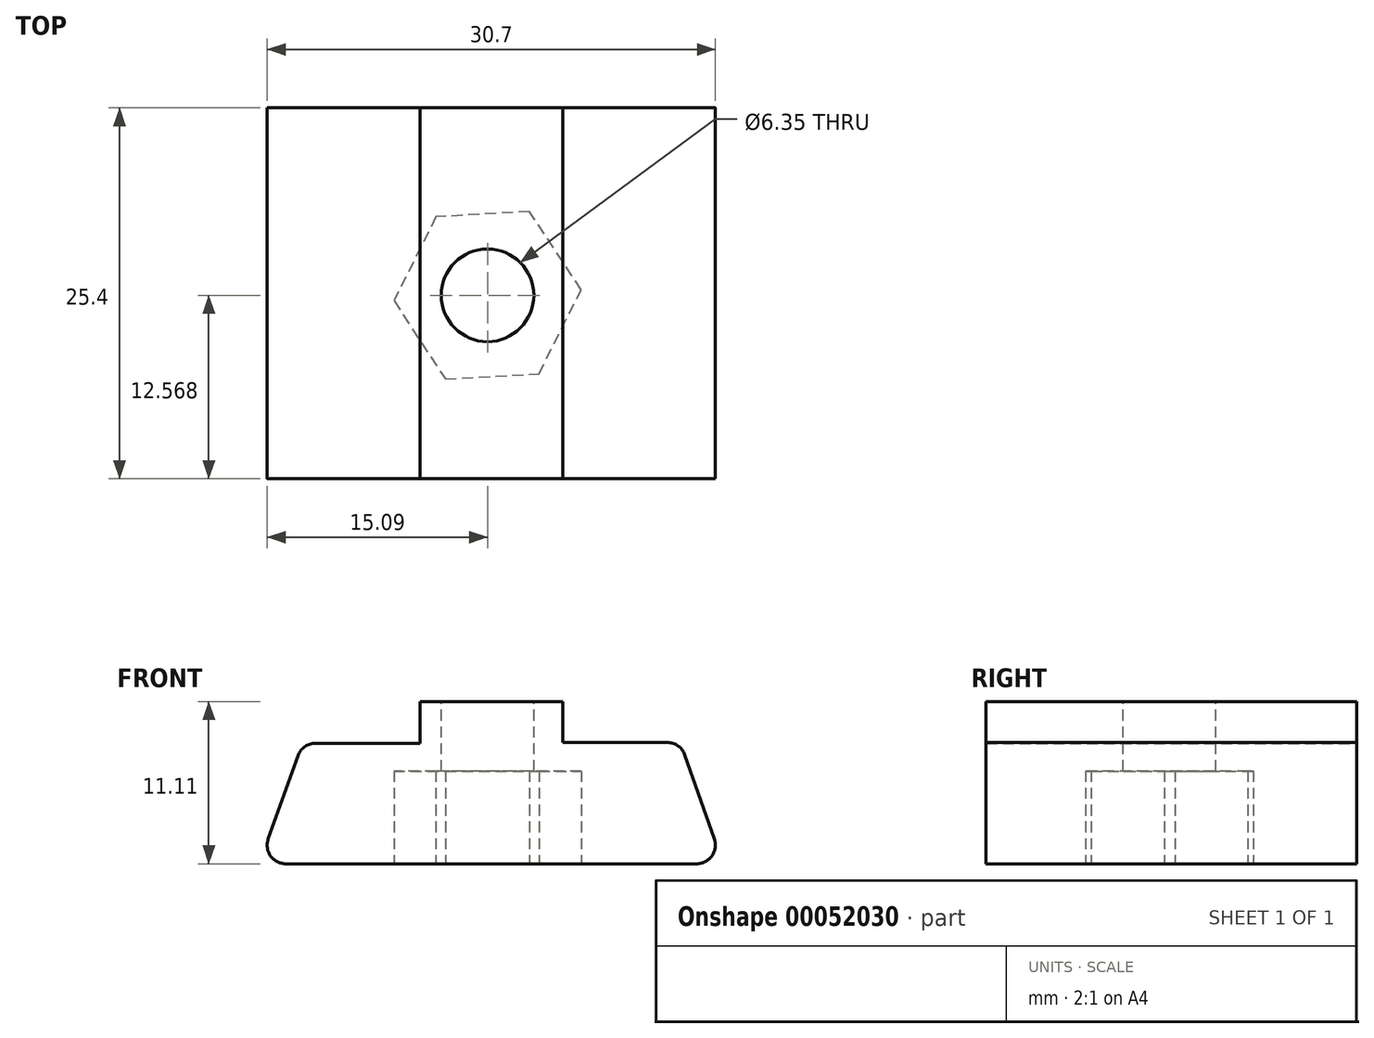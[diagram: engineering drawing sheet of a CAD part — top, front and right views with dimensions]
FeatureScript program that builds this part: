
annotation { "Feature Type Name" : "Feature", "Feature Type Description" : "" }
export const myFeature = defineFeature(function(context is Context, id is Id, definition is map)
    precondition{}
    {
        {
            var Q0;
            Q0=qCreatedBy(makeId("Front.planeOp"),FACE);
            var sketch = newSketch(context, id + "F0", { "sketchPlane" : qUnion([Q0])});
            skLineSegment(sketch, "E0", {"start": v(-15.62, 0) * mm, "end": v(16.13, 0) * mm});
            skLineSegment(sketch, "E1", {"start": v(16.13, 0) * mm, "end": v(13.23, 8.3) * mm});
            skLineSegment(sketch, "E2", {"start": v(13.23, 8.3) * mm, "end": v(5.16, 8.3) * mm});
            skLineSegment(sketch, "E3", {"start": v(5.16, 8.3) * mm, "end": v(5.16, 11.11) * mm});
            skLineSegment(sketch, "E4", {"start": v(5.16, 11.11) * mm, "end": v(-4.62, 11.11) * mm});
            skLineSegment(sketch, "E5", {"start": v(-4.62, 11.11) * mm, "end": v(-4.62, 8.26) * mm});
            skLineSegment(sketch, "E6", {"start": v(-4.62, 8.26) * mm, "end": v(-12.68, 8.25) * mm});
            skLineSegment(sketch, "E7", {"start": v(-12.68, 8.26) * mm, "end": v(-15.62, 0) * mm});
            skSolve(sketch);
        }
        {
            var Q0;
            Q0 = qSketchRegion(id + "F0", true);
            extrude(context, id + "F1", {"entities" : qUnion([Q0]), "depth" : 25.4 * mm});
        }
        {
            var Q0;
            Q0=makeQuery(id+"F1.opExtrude","SWEPT_FACE",FACE,{"disambiguationData":[OSD([sQuery(id+"F0.wireOp",EDGE,"E4")])]});
            var sketch = newSketch(context, id + "F2", { "sketchPlane" : qUnion([Q0])});
            skCircle(sketch, "E8", {"center": v(0, -12.83) * mm, "radius": 2.25 * mm});
            skSolve(sketch);
        }
        {
            var Q0;
            Q0=sQuery(id+"F2.wireOp",VERTEX,"E8.center");
            var Q1;
            Q1=makeQuery(id+"F1.opExtrude","SWEPT_BODY",BODY,{"disambiguationData":[OSD([sQuery(id+"F0.wireOp",EDGE,"E0"),sQuery(id+"F0.wireOp",EDGE,"E1"),sQuery(id+"F0.wireOp",EDGE,"E2"),sQuery(id+"F0.wireOp",EDGE,"E3"),sQuery(id+"F0.wireOp",EDGE,"E4"),sQuery(id+"F0.wireOp",EDGE,"E5"),sQuery(id+"F0.wireOp",EDGE,"E6"),sQuery(id+"F0.wireOp",EDGE,"E7")])]});
            hole(context, id + "F3", {"style" : HoleStyle.SIMPLE, "holeDiameter" : 6.35 * mm, "endStyle" : HoleEndStyle.THROUGH, "locations" : qUnion([Q0]), "scope" : qUnion([Q1])});
        }
        {
            var Q0;
            Q0=makeQuery(id+"F1.opExtrude","SWEPT_FACE",FACE,{"disambiguationData":[OSD([sQuery(id+"F0.wireOp",EDGE,"E0")])]});
            var sketch = newSketch(context, id + "F4", { "sketchPlane" : qUnion([Q0])});
            skCircle(sketch, "E9.cCircle", {"center": v(0, 12.83) * mm, "radius": 6.42 * mm, "construction": true});
            skLineSegment(sketch, "E9.0", {"start": v(-3.53, 7.46) * mm, "end": v(-6.41, 13.2) * mm});
            skLineSegment(sketch, "E9.1", {"start": v(-6.41, 13.2) * mm, "end": v(-2.89, 18.57) * mm});
            skLineSegment(sketch, "E9.2", {"start": v(-2.89, 18.57) * mm, "end": v(3.53, 18.2) * mm});
            skLineSegment(sketch, "E9.3", {"start": v(3.53, 18.2) * mm, "end": v(6.41, 12.46) * mm});
            skLineSegment(sketch, "E9.4", {"start": v(6.41, 12.46) * mm, "end": v(2.89, 7.1) * mm});
            skLineSegment(sketch, "E9.5", {"start": v(2.89, 7.1) * mm, "end": v(-3.53, 7.46) * mm});
            skSolve(sketch);
        }
        {
            var Q0;
            Q0=makeQuery(id+"F4.imprint","IMPRINT",FACE,{"disambiguationData":[TD([[makeQuery(id+"F4.imprint","IMPRINT",EDGE,{"derivedFrom":makeQuery(id+"F3.hole-0.boolean.opBoolean","INTERSECT",EDGE,{"derivedFrom":[makeQuery(id+"F1.opExtrude","SWEPT_FACE",FACE,{"disambiguationData":[OSD([sQuery(id+"F0.wireOp",EDGE,"E0")])]}),makeQuery(id+"F3.hole-0.opRevolve","SWEPT_FACE",FACE,{"disambiguationData":[OSD([sQuery(id+"F3.hole-0.sketch.wireOp",EDGE,"core_line_2")])]})]})}),1.0]])]});
            var Q1;
            Q1=makeQuery(id+"F4.imprint","IMPRINT",FACE,{"disambiguationData":[TD([[makeQuery(id+"F4.imprint","IMPRINT",EDGE,{"derivedFrom":sQuery(id+"F4.wireOp",EDGE,"E9.0")}),-1.0]])]});
            extrude(context, id + "F5", {"entities" : qUnion([Q0, Q1]), "operationType" : NewBodyOperationType.REMOVE, "oppositeDirection" : true, "depth" : 6.35 * mm});
        }
        {
            var Q0;
            Q0=makeQuery(id+"F1.opExtrude","SWEPT_EDGE",EDGE,{"disambiguationData":[OSD([sQuery(id+"F0.wireOp",EDGE,"E0"),sQuery(id+"F0.wireOp",EDGE,"E1")])]});
            var Q1;
            Q1=makeQuery(id+"F1.opExtrude","SWEPT_EDGE",EDGE,{"disambiguationData":[OSD([sQuery(id+"F0.wireOp",EDGE,"E0"),sQuery(id+"F0.wireOp",EDGE,"E7")])]});
            var Q2;
            Q2=makeQuery(id+"F1.opExtrude","SWEPT_EDGE",EDGE,{"disambiguationData":[OSD([sQuery(id+"F0.wireOp",EDGE,"E1"),sQuery(id+"F0.wireOp",EDGE,"E2")])]});
            var Q3;
            Q3=makeQuery(id+"F1.opExtrude","SWEPT_EDGE",EDGE,{"disambiguationData":[OSD([sQuery(id+"F0.wireOp",EDGE,"E6"),sQuery(id+"F0.wireOp",EDGE,"E7")])]});
            fillet(context, id + "F6", {"entities" : qUnion([Q0, Q1, Q2, Q3]), "radius" : 1.27 * mm, "tangentPropagation" : true, "allowEdgeOverflow" : false});
        }
    });
